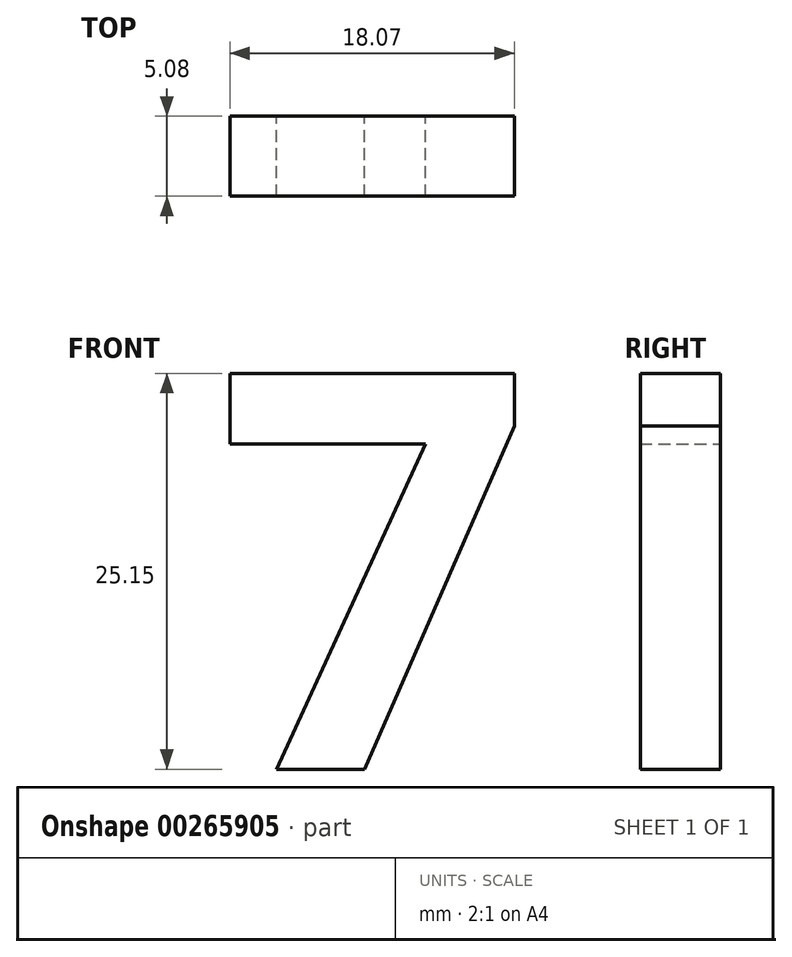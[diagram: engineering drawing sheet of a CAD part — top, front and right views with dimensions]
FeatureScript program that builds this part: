
annotation { "Feature Type Name" : "Feature", "Feature Type Description" : "" }
export const myFeature = defineFeature(function(context is Context, id is Id, definition is map)
    precondition{}
    {
        {
            var Q0;
            Q0=qCreatedBy(makeId("Front.planeOp"),FACE);
            var sketch = newSketch(context, id + "F0", { "sketchPlane" : qUnion([Q0])});
            skText(sketch, "E0", { "text": "7", "fontName": "OpenSans-Bold.ttf"});
            const initialGuessF0  = {"E0": [-0.02205, -0.00237, 1, 0, 0.0254]};
            skSetInitialGuess(sketch, initialGuessF0);
            skSolve(sketch);
        }
        {
            var Q0;
            Q0 = qSketchRegion(id + "F0", true);
            extrude(context, id + "F1", {"entities" : qUnion([Q0]), "depth" : 5.08 * mm});
        }
    });
